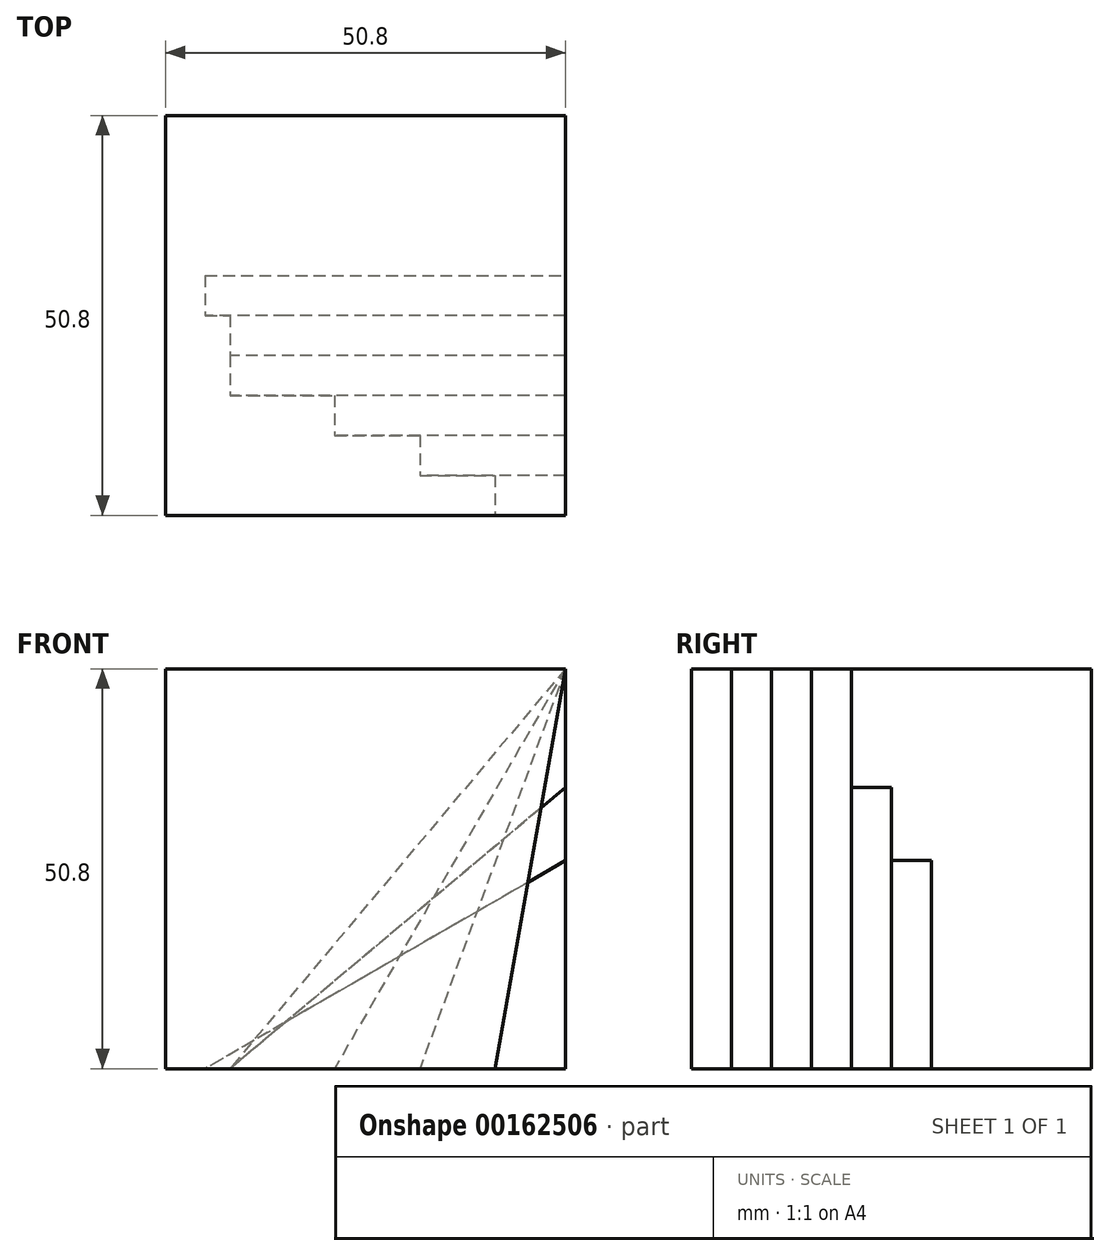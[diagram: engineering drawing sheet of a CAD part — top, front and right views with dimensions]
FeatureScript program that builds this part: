
annotation { "Feature Type Name" : "Feature", "Feature Type Description" : "" }
export const myFeature = defineFeature(function(context is Context, id is Id, definition is map)
    precondition{}
    {
        {
            var Q0;
            Q0=qCreatedBy(makeId("Front.planeOp"),FACE);
            var sketch = newSketch(context, id + "F0", { "sketchPlane" : qUnion([Q0])});
            skLineSegment(sketch, "E0.bottom", {"start": v(-25.4, 25.4) * mm, "end": v(25.4, 25.4) * mm});
            skLineSegment(sketch, "E0.top", {"start": v(-25.4, -25.4) * mm, "end": v(25.4, -25.4) * mm});
            skLineSegment(sketch, "E0.left", {"start": v(-25.4, 25.4) * mm, "end": v(-25.4, -25.4) * mm});
            skLineSegment(sketch, "E0.right", {"start": v(25.4, 25.4) * mm, "end": v(25.4, -25.4) * mm});
            skPoint(sketch, "E0.middle", {"position": v(0, 0) * mm});
            skSolve(sketch);
        }
        {
            var Q0;
            Q0 = qSketchRegion(id + "F0", true);
            extrude(context, id + "F1", {"entities" : qUnion([Q0]), "depth" : 50.8 * mm});
        }
        {
            var Q0;
            Q0=makeQuery(id+"F1.opExtrude","CAP_FACE",FACE,{"disambiguationData":[OSD([sQuery(id+"F0.wireOp",EDGE,"E0.bottom"),sQuery(id+"F0.wireOp",EDGE,"E0.top"),sQuery(id+"F0.wireOp",EDGE,"E0.left"),sQuery(id+"F0.wireOp",EDGE,"E0.right")])],"isStart":false});
            var sketch = newSketch(context, id + "F2", { "sketchPlane" : qUnion([Q0])});
            skLineSegment(sketch, "E1", {"start": v(25.4, 25.4) * mm, "end": v(16.44, -25.4) * mm});
            skLineSegment(sketch, "E2", {"start": v(16.44, -25.4) * mm, "end": v(31, -25.4) * mm});
            skLineSegment(sketch, "E3", {"start": v(31, -25.4) * mm, "end": v(31, 25.4) * mm});
            skLineSegment(sketch, "E4", {"start": v(31, 25.4) * mm, "end": v(25.4, 25.4) * mm});
            skSolve(sketch);
        }
        {
            var Q0;
            Q0 = qSketchRegion(id + "F2", true);
            extrude(context, id + "F3", {"entities" : qUnion([Q0]), "operationType" : NewBodyOperationType.REMOVE, "oppositeDirection" : true, "depth" : 5.08 * mm});
        }
        {
            var Q0;
            Q0=makeQuery(id+"F3.boolean.opBoolean","COPY",FACE,{"derivedFrom":makeQuery(id+"F3.opExtrude","CAP_FACE",FACE,{"disambiguationData":[OSD([sQuery(id+"F2.wireOp",EDGE,"E1"),sQuery(id+"F2.wireOp",EDGE,"E2"),sQuery(id+"F2.wireOp",EDGE,"E3"),sQuery(id+"F2.wireOp",EDGE,"E4")])],"isStart":false})});
            var sketch = newSketch(context, id + "F4", { "sketchPlane" : qUnion([Q0])});
            skLineSegment(sketch, "E5", {"start": v(25.4, 25.4) * mm, "end": v(6.63, -26.18) * mm});
            skLineSegment(sketch, "E6", {"start": v(6.63, -26.18) * mm, "end": v(32.86, -26.18) * mm});
            skLineSegment(sketch, "E7", {"start": v(32.86, -26.18) * mm, "end": v(32.86, 25.4) * mm});
            skLineSegment(sketch, "E8", {"start": v(32.86, 25.4) * mm, "end": v(25.4, 25.4) * mm});
            skSolve(sketch);
        }
        {
            var Q0;
            Q0 = qSketchRegion(id + "F4", true);
            extrude(context, id + "F5", {"entities" : qUnion([Q0]), "operationType" : NewBodyOperationType.REMOVE, "oppositeDirection" : true, "depth" : 5.08 * mm});
        }
        {
            var Q0;
            Q0=makeQuery(id+"F5.boolean.opBoolean","COPY",FACE,{"derivedFrom":makeQuery(id+"F5.opExtrude","CAP_FACE",FACE,{"disambiguationData":[OSD([sQuery(id+"F4.wireOp",EDGE,"E5"),sQuery(id+"F4.wireOp",EDGE,"E6"),sQuery(id+"F4.wireOp",EDGE,"E7"),sQuery(id+"F4.wireOp",EDGE,"E8")])],"isStart":false})});
            var sketch = newSketch(context, id + "F6", { "sketchPlane" : qUnion([Q0])});
            skLineSegment(sketch, "E9", {"start": v(25.4, 25.4) * mm, "end": v(-7.15, -30.98) * mm});
            skLineSegment(sketch, "E10", {"start": v(-7.15, -30.98) * mm, "end": v(35.19, -30.98) * mm});
            skLineSegment(sketch, "E11", {"start": v(35.19, -30.98) * mm, "end": v(35.19, 25.4) * mm});
            skLineSegment(sketch, "E12", {"start": v(35.19, 25.4) * mm, "end": v(25.4, 25.4) * mm});
            skSolve(sketch);
        }
        {
            var Q0;
            Q0 = qSketchRegion(id + "F6", true);
            extrude(context, id + "F7", {"entities" : qUnion([Q0]), "operationType" : NewBodyOperationType.REMOVE, "oppositeDirection" : true, "depth" : 5.08 * mm});
        }
        {
            var Q0;
            Q0=makeQuery(id+"F7.boolean.opBoolean","COPY",FACE,{"derivedFrom":makeQuery(id+"F7.opExtrude","CAP_FACE",FACE,{"disambiguationData":[OSD([sQuery(id+"F6.wireOp",EDGE,"E9"),sQuery(id+"F6.wireOp",EDGE,"E10"),sQuery(id+"F6.wireOp",EDGE,"E11"),sQuery(id+"F6.wireOp",EDGE,"E12")])],"isStart":false})});
            var sketch = newSketch(context, id + "F8", { "sketchPlane" : qUnion([Q0])});
            skLineSegment(sketch, "E13", {"start": v(25.4, 25.4) * mm, "end": v(-24.74, -34.35) * mm});
            skLineSegment(sketch, "E14", {"start": v(-24.74, -34.35) * mm, "end": v(63.2, -34.35) * mm});
            skLineSegment(sketch, "E15", {"start": v(63.2, -34.35) * mm, "end": v(63.2, 25.4) * mm});
            skLineSegment(sketch, "E16", {"start": v(63.2, 25.4) * mm, "end": v(25.4, 25.4) * mm});
            skSolve(sketch);
        }
        {
            var Q0;
            Q0 = qSketchRegion(id + "F8", true);
            extrude(context, id + "F9", {"entities" : qUnion([Q0]), "operationType" : NewBodyOperationType.REMOVE, "oppositeDirection" : true, "depth" : 5.08 * mm});
        }
        {
            var Q0;
            Q0=makeQuery(id+"F9.boolean.opBoolean","COPY",FACE,{"derivedFrom":makeQuery(id+"F9.opExtrude","CAP_FACE",FACE,{"disambiguationData":[OSD([sQuery(id+"F8.wireOp",EDGE,"E13"),sQuery(id+"F8.wireOp",EDGE,"E14"),sQuery(id+"F8.wireOp",EDGE,"E15"),sQuery(id+"F8.wireOp",EDGE,"E16")])],"isStart":false})});
            var sketch = newSketch(context, id + "F10", { "sketchPlane" : qUnion([Q0])});
            skLineSegment(sketch, "E17", {"start": v(43.35, 25.4) * mm, "end": v(-33.32, -38.93) * mm});
            skLineSegment(sketch, "E18", {"start": v(-33.32, -38.93) * mm, "end": v(66.86, -38.93) * mm});
            skLineSegment(sketch, "E19", {"start": v(66.86, -38.93) * mm, "end": v(66.86, 25.4) * mm});
            skLineSegment(sketch, "E20", {"start": v(66.86, 25.4) * mm, "end": v(43.35, 25.4) * mm});
            skSolve(sketch);
        }
        {
            var Q0;
            Q0 = qSketchRegion(id + "F10", true);
            extrude(context, id + "F11", {"entities" : qUnion([Q0]), "operationType" : NewBodyOperationType.REMOVE, "oppositeDirection" : true, "depth" : 5.08 * mm});
        }
        {
            var Q0;
            Q0=makeQuery(id+"F11.boolean.opBoolean","COPY",FACE,{"derivedFrom":makeQuery(id+"F11.opExtrude","CAP_FACE",FACE,{"disambiguationData":[OSD([sQuery(id+"F10.wireOp",EDGE,"E17"),sQuery(id+"F10.wireOp",EDGE,"E18"),sQuery(id+"F10.wireOp",EDGE,"E19"),sQuery(id+"F10.wireOp",EDGE,"E20")])],"isStart":false})});
            var sketch = newSketch(context, id + "F12", { "sketchPlane" : qUnion([Q0])});
            skLineSegment(sketch, "E21", {"start": v(44.7, 12.18) * mm, "end": v(-34.9, -33.78) * mm});
            skLineSegment(sketch, "E22", {"start": v(-34.9, -33.78) * mm, "end": v(62.78, -33.78) * mm});
            skLineSegment(sketch, "E23", {"start": v(62.78, -33.78) * mm, "end": v(62.78, 12.18) * mm});
            skLineSegment(sketch, "E24", {"start": v(62.78, 12.18) * mm, "end": v(44.7, 12.18) * mm});
            skSolve(sketch);
        }
        {
            var Q0;
            Q0 = qSketchRegion(id + "F12", true);
            extrude(context, id + "F13", {"entities" : qUnion([Q0]), "operationType" : NewBodyOperationType.REMOVE, "oppositeDirection" : true, "depth" : 5.08 * mm});
        }
    });
